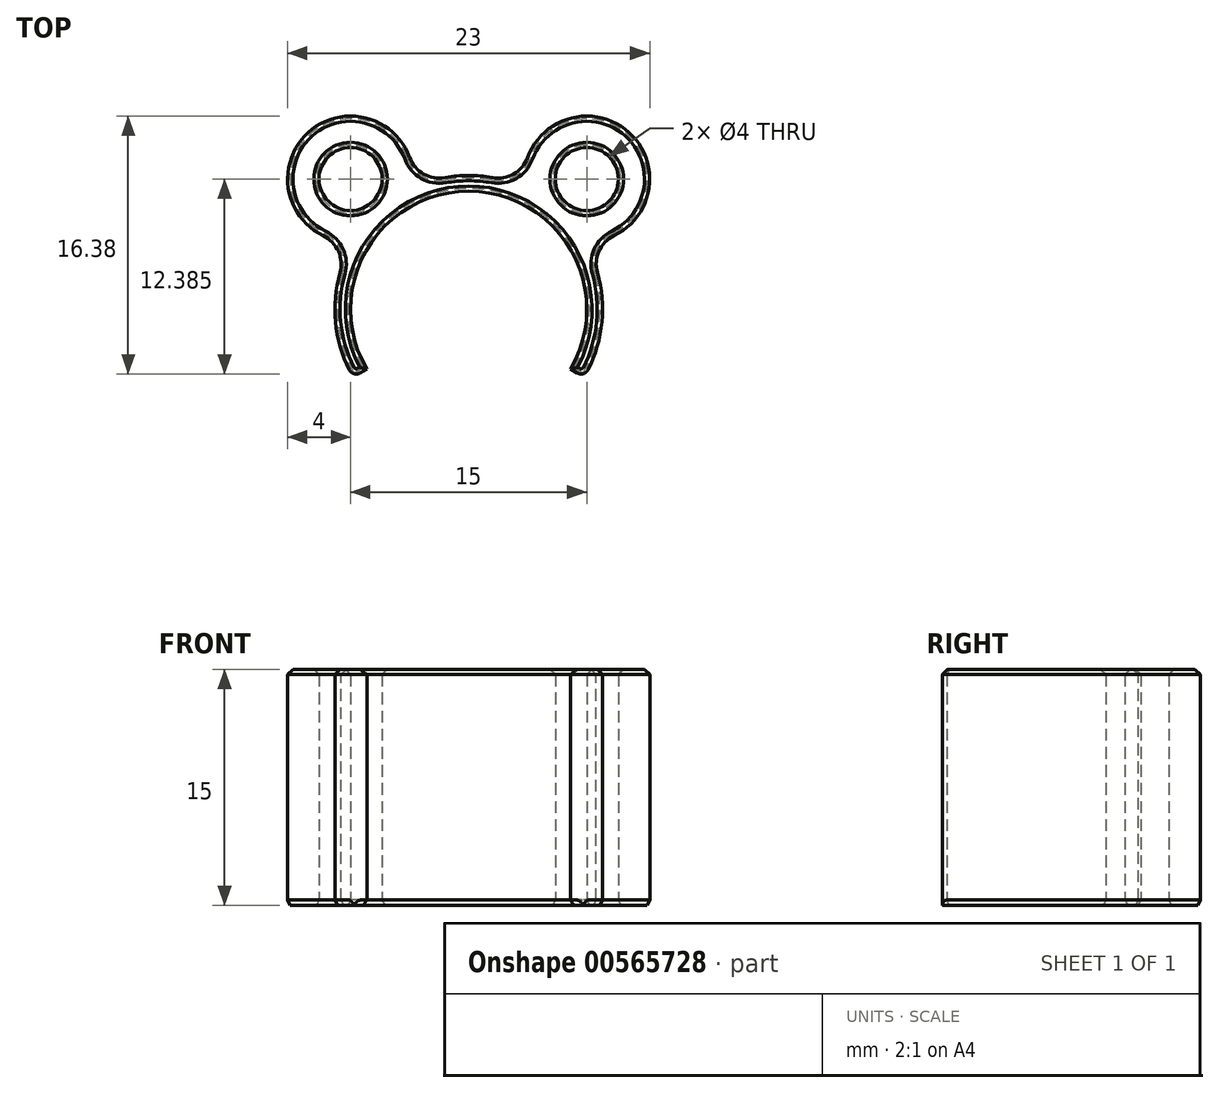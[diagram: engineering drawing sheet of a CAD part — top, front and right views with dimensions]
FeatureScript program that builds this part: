
annotation { "Feature Type Name" : "Feature", "Feature Type Description" : "" }
export const myFeature = defineFeature(function(context is Context, id is Id, definition is map)
    precondition{}
    {
        {
            var Q0;
            Q0=qCreatedBy(makeId("Top.planeOp"),FACE);
            var sketch = newSketch(context, id + "F0", { "sketchPlane" : qUnion([Q0])});
            skArc(sketch, "E0", {"start": v(6.47, -3.8) * mm, "mid": v(0, 7.5) * mm, "end": v(-6.47, -3.8) * mm});
            skArc(sketch, "E1", {"start": v(3.54, 7.73) * mm, "mid": v(0, 8.5) * mm, "end": v(-3.54, 7.73) * mm});
            skLineSegment(sketch, "E2", {"start": v(0, 0) * mm, "end": v(0, 19) * mm});
            skCircle(sketch, "E3", {"center": v(7.5, 8.27) * mm, "radius": 2 * mm});
            skArc(sketch, "E4.0", {"start": v(7.35, 4.28) * mm, "mid": v(10.19, 11.24) * mm, "end": v(3.54, 7.73) * mm});
            skArc(sketch, "E5.MirrorCS", {"start": v(-7.35, 4.28) * mm, "mid": v(-10.19, 11.24) * mm, "end": v(-3.54, 7.73) * mm});
            skCircle(sketch, "E6.MirrorC", {"center": v(-7.5, 8.27) * mm, "radius": 2 * mm});
            skArc(sketch, "E7.trimOffspring", {"start": v(-7.35, 4.28) * mm, "mid": v(-8.5, -0.02) * mm, "end": v(-7.33, -4.3) * mm});
            skLineSegment(sketch, "E8", {"start": v(-7.33, -4.3) * mm, "end": v(0, 0) * mm});
            skLineSegment(sketch, "E9", {"start": v(0, 0) * mm, "end": v(7.33, -4.3) * mm});
            skArc(sketch, "E10.trimOffspring", {"start": v(7.33, -4.3) * mm, "mid": v(8.5, -0.02) * mm, "end": v(7.35, 4.28) * mm});
            skSolve(sketch);
        }
        {
            var Q0;
            Q0=makeQuery(id+"F0.imprint","IMPRINT",FACE,{"disambiguationData":[TD([[makeQuery(id+"F0.imprint","IMPRINT",EDGE,{"derivedFrom":sQuery(id+"F0.wireOp",EDGE,"E0")}),-1.0]])]});
            extrude(context, id + "F1", {"entities" : qUnion([Q0]), "depth" : 15 * mm, "offsetDistance" : 25 * mm});
        }
        {
            var Q0;
            Q0=makeQuery(id+"F1.opExtrude","SWEPT_EDGE",EDGE,{"disambiguationData":[OSD([sQuery(id+"F0.wireOp",EDGE,"E4.0"),sQuery(id+"F0.wireOp",EDGE,"E10.trimOffspring")])]});
            var Q1;
            Q1=makeQuery(id+"F1.opExtrude","SWEPT_EDGE",EDGE,{"disambiguationData":[OSD([sQuery(id+"F0.wireOp",EDGE,"E1"),sQuery(id+"F0.wireOp",EDGE,"E4.0")])]});
            var Q2;
            Q2=makeQuery(id+"F1.opExtrude","SWEPT_EDGE",EDGE,{"disambiguationData":[OSD([sQuery(id+"F0.wireOp",EDGE,"E1"),sQuery(id+"F0.wireOp",EDGE,"E5.MirrorCS")])]});
            var Q3;
            Q3=makeQuery(id+"F1.opExtrude","SWEPT_EDGE",EDGE,{"disambiguationData":[OSD([sQuery(id+"F0.wireOp",EDGE,"E5.MirrorCS"),sQuery(id+"F0.wireOp",EDGE,"E7.trimOffspring")])]});
            fillet(context, id + "F2", {"entities" : qUnion([Q0, Q1, Q2, Q3]), "radius" : 2 * mm, "tangentPropagation" : true, "allowEdgeOverflow" : false});
        }
        {
            var Q0;
            Q0=makeQuery(id+"F1.opExtrude","CAP_FACE",FACE,{"disambiguationData":[OSD([sQuery(id+"F0.wireOp",EDGE,"E0"),sQuery(id+"F0.wireOp",EDGE,"E1"),sQuery(id+"F0.wireOp",EDGE,"E3"),sQuery(id+"F0.wireOp",EDGE,"E4.0"),sQuery(id+"F0.wireOp",EDGE,"E5.MirrorCS"),sQuery(id+"F0.wireOp",EDGE,"E6.MirrorC"),sQuery(id+"F0.wireOp",EDGE,"E7.trimOffspring"),sQuery(id+"F0.wireOp",EDGE,"E8"),sQuery(id+"F0.wireOp",EDGE,"E9"),sQuery(id+"F0.wireOp",EDGE,"E10.trimOffspring")])],"isStart":true});
            chamfer(context, id + "F3", {"entities" : qUnion([Q0]), "chamferType" : ChamferType.TWO_OFFSETS, "width1" : .167 * mm, "oppositeDirection" : false, "width2" : .334 * mm, "tangentPropagation" : true});
        }
        {
            var Q0;
            Q0=makeQuery(id+"F1.opExtrude","SWEPT_EDGE",EDGE,{"disambiguationData":[OSD([sQuery(id+"F0.wireOp",EDGE,"E7.trimOffspring"),sQuery(id+"F0.wireOp",EDGE,"E8")])]});
            var Q1;
            Q1=makeQuery(id+"F1.opExtrude","SWEPT_EDGE",EDGE,{"disambiguationData":[OSD([sQuery(id+"F0.wireOp",EDGE,"E9"),sQuery(id+"F0.wireOp",EDGE,"E10.trimOffspring")])]});
            fillet(context, id + "F4", {"entities" : qUnion([Q0, Q1]), "radius" : .5 * mm, "tangentPropagation" : true, "allowEdgeOverflow" : false});
        }
        {
            var Q0;
            Q0=makeQuery(id+"F1.opExtrude","CAP_FACE",FACE,{"disambiguationData":[OSD([sQuery(id+"F0.wireOp",EDGE,"E0"),sQuery(id+"F0.wireOp",EDGE,"E1"),sQuery(id+"F0.wireOp",EDGE,"E3"),sQuery(id+"F0.wireOp",EDGE,"E4.0"),sQuery(id+"F0.wireOp",EDGE,"E5.MirrorCS"),sQuery(id+"F0.wireOp",EDGE,"E6.MirrorC"),sQuery(id+"F0.wireOp",EDGE,"E7.trimOffspring"),sQuery(id+"F0.wireOp",EDGE,"E8"),sQuery(id+"F0.wireOp",EDGE,"E9"),sQuery(id+"F0.wireOp",EDGE,"E10.trimOffspring")])],"isStart":false});
            chamfer(context, id + "F5", {"entities" : qUnion([Q0]), "width" : .334 * mm, "tangentPropagation" : true});
        }
    });
